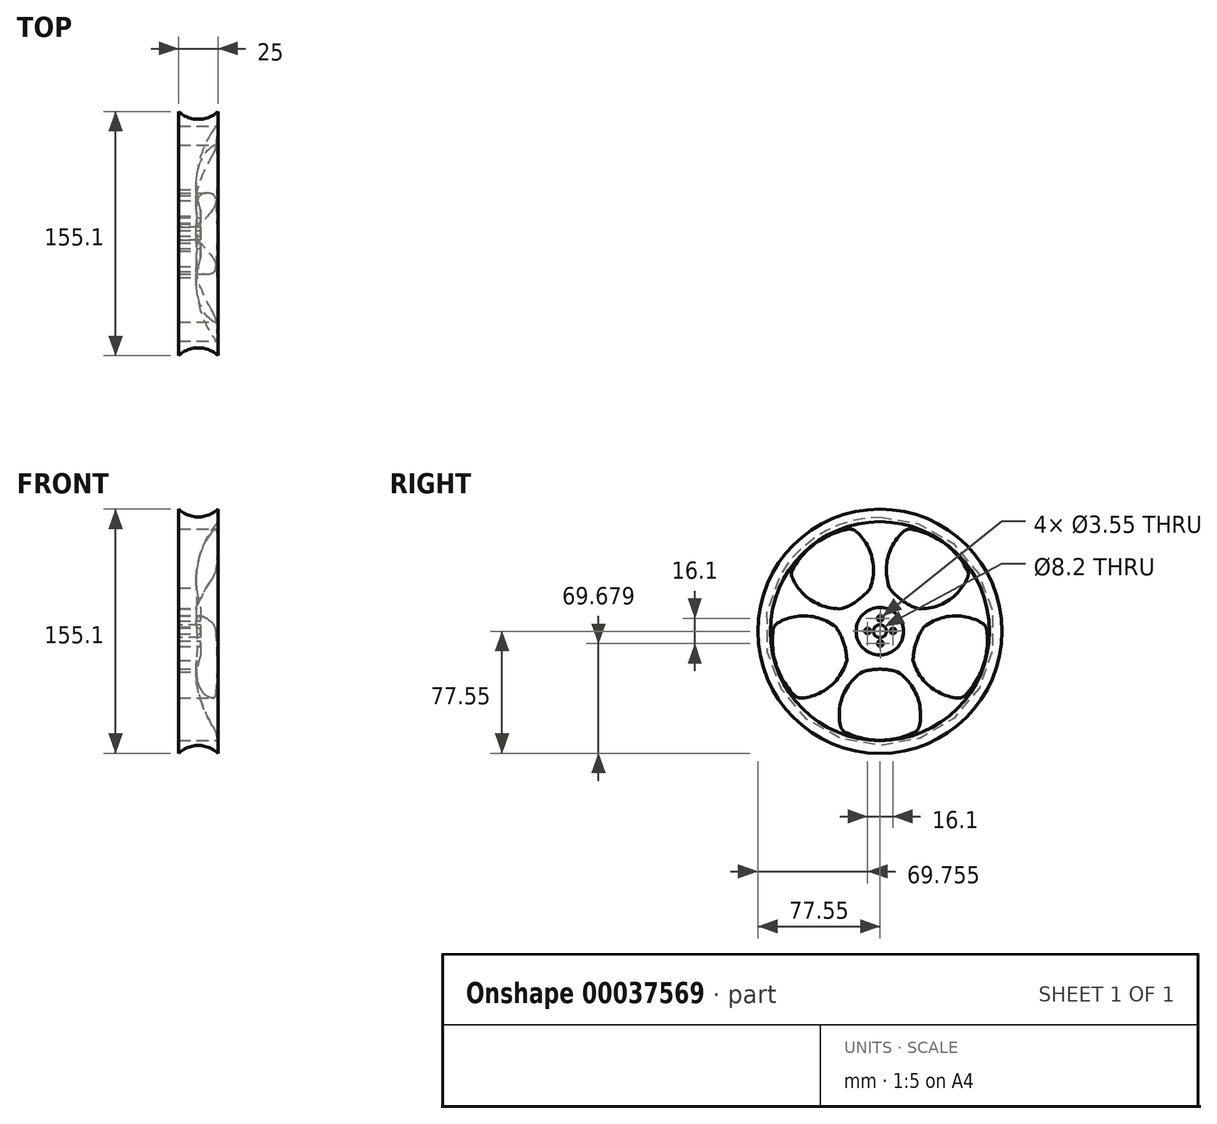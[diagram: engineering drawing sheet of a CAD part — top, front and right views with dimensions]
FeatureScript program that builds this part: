
annotation { "Feature Type Name" : "Feature", "Feature Type Description" : "" }
export const myFeature = defineFeature(function(context is Context, id is Id, definition is map)
    precondition{}
    {
        {
            var Q0;
            Q0=qCreatedBy(makeId("Top.planeOp"),FACE);
            var sketch = newSketch(context, id + "F0", { "sketchPlane" : qUnion([Q0])});
            skLineSegment(sketch, "E0", {"start": v(-41.62, 0) * mm, "end": v(49.27, 0) * mm, "construction": true});
            skLineSegment(sketch, "E1", {"start": v(0, 0) * mm, "end": v(0, 26.1) * mm, "construction": true});
            skLineSegment(sketch, "E2", {"start": v(-10.94, 77.55) * mm, "end": v(-10.94, 4.1) * mm});
            skArc(sketch, "E3", {"start": v(-10.94, 77.55) * mm, "mid": v(1.56, 72.59) * mm, "end": v(14.06, 77.55) * mm});
            skLineSegment(sketch, "E4", {"start": v(14.06, 77.55) * mm, "end": v(14.06, 69.55) * mm});
            skArc(sketch, "E5", {"start": v(14.06, 69.55) * mm, "mid": v(1.38, 43.78) * mm, "end": v(3.06, 15.1) * mm});
            skLineSegment(sketch, "E6", {"start": v(3.06, 15.1) * mm, "end": v(3.06, 4.1) * mm});
            skLineSegment(sketch, "E7", {"start": v(3.06, 4.1) * mm, "end": v(-10.94, 4.1) * mm});
            skSolve(sketch);
        }
        {
            var Q0;
            Q0=makeQuery(id+"F0.imprint","IMPRINT",FACE,{"disambiguationData":[TD([[makeQuery(id+"F0.imprint","IMPRINT",EDGE,{"derivedFrom":sQuery(id+"F0.wireOp",EDGE,"E2")}),1.0]])]});
            var Q1;
            Q1=sQuery(id+"F0.wireOp",EDGE,"E0");
            revolve(context, id + "F1", {"entities" : qUnion([Q0]), "axis" : qUnion([Q1]), "revolveType" : RevolveType.FULL});
        }
        {
            var Q0;
            Q0=qCreatedBy(makeId("Right.planeOp"),FACE);
            cPlane(context, id + "F2", {"entities" : qUnion([Q0]), "cplaneType" : CPlaneType.OFFSET, "offset" : 15 * mm, "width" : 150 * mm, "height" : 150 * mm});
        }
        {
            var Q0;
            Q0=qCreatedBy(id+"F2.planeOp",FACE);
            var sketch = newSketch(context, id + "F3", { "sketchPlane" : qUnion([Q0])});
            skArc(sketch, "E8", {"start": v(-11.09, -25.74) * mm, "mid": v(-23.44, -40.77) * mm, "end": v(-25.05, -60.15) * mm});
            skArc(sketch, "E9.MirrorCS", {"start": v(11.09, -25.74) * mm, "mid": v(23.44, -40.77) * mm, "end": v(25.05, -60.15) * mm});
            skArc(sketch, "E10", {"start": v(11.09, -25.74) * mm, "mid": v(0, -24.1) * mm, "end": v(-11.09, -25.74) * mm});
            skArc(sketch, "E11", {"start": v(-21.8, -64.25) * mm, "mid": v(0, -69.23) * mm, "end": v(21.8, -64.25) * mm});
            skPoint(sketch, "E12.visualSharp", {"position": v(-24.29, -62.96) * mm});
            skArc(sketch, "E12.filletArc", {"start": v(-25.05, -60.15) * mm, "mid": v(-23.9, -62.57) * mm, "end": v(-21.8, -64.25) * mm});
            skPoint(sketch, "E13.visualSharp", {"position": v(24.29, -62.96) * mm});
            skArc(sketch, "E13.filletArc", {"start": v(21.8, -64.25) * mm, "mid": v(23.9, -62.57) * mm, "end": v(25.05, -60.15) * mm});
            skArc(sketch, "E14.1.0", {"start": v(27.9, 2.6) * mm, "mid": v(22.92, -7.45) * mm, "end": v(21.05, -18.5) * mm});
            skArc(sketch, "E14.1.1", {"start": v(27.9, 2.6) * mm, "mid": v(46.01, 9.7) * mm, "end": v(64.95, 5.23) * mm});
            skArc(sketch, "E14.1.2", {"start": v(54.37, -40.59) * mm, "mid": v(65.84, -21.4) * mm, "end": v(67.84, 0.88) * mm});
            skArc(sketch, "E14.1.3", {"start": v(21.05, -18.5) * mm, "mid": v(31.53, -34.89) * mm, "end": v(49.47, -42.4) * mm});
            skArc(sketch, "E14.1.4", {"start": v(67.84, 0.88) * mm, "mid": v(66.9, 3.39) * mm, "end": v(64.95, 5.23) * mm});
            skArc(sketch, "E14.1.5", {"start": v(49.47, -42.4) * mm, "mid": v(52.13, -42.06) * mm, "end": v(54.37, -40.59) * mm});
            skArc(sketch, "E14.2.0", {"start": v(6.16, 27.34) * mm, "mid": v(14.16, 19.5) * mm, "end": v(24.1, 14.3) * mm});
            skArc(sketch, "E14.2.1", {"start": v(6.16, 27.34) * mm, "mid": v(5, 46.76) * mm, "end": v(15.1, 63.39) * mm});
            skArc(sketch, "E14.2.2", {"start": v(55.4, 39.17) * mm, "mid": v(40.7, 56) * mm, "end": v(20.13, 64.8) * mm});
            skArc(sketch, "E14.2.3", {"start": v(24.1, 14.3) * mm, "mid": v(42.92, 19.2) * mm, "end": v(55.62, 33.94) * mm});
            skArc(sketch, "E14.2.4", {"start": v(20.13, 64.8) * mm, "mid": v(17.45, 64.67) * mm, "end": v(15.1, 63.39) * mm});
            skArc(sketch, "E14.2.5", {"start": v(55.62, 33.94) * mm, "mid": v(56.1, 36.58) * mm, "end": v(55.4, 39.17) * mm});
            skArc(sketch, "E14.3.0", {"start": v(-24.1, 14.3) * mm, "mid": v(-14.16, 19.5) * mm, "end": v(-6.16, 27.34) * mm});
            skArc(sketch, "E14.3.1", {"start": v(-24.1, 14.3) * mm, "mid": v(-42.92, 19.2) * mm, "end": v(-55.62, 33.94) * mm});
            skArc(sketch, "E14.3.2", {"start": v(-20.13, 64.8) * mm, "mid": v(-40.7, 56) * mm, "end": v(-55.4, 39.17) * mm});
            skArc(sketch, "E14.3.3", {"start": v(-6.16, 27.34) * mm, "mid": v(-5, 46.76) * mm, "end": v(-15.1, 63.39) * mm});
            skArc(sketch, "E14.3.4", {"start": v(-55.4, 39.17) * mm, "mid": v(-56.1, 36.58) * mm, "end": v(-55.62, 33.94) * mm});
            skArc(sketch, "E14.3.5", {"start": v(-15.1, 63.39) * mm, "mid": v(-17.45, 64.67) * mm, "end": v(-20.13, 64.8) * mm});
            skArc(sketch, "E14.4.0", {"start": v(-21.05, -18.5) * mm, "mid": v(-22.92, -7.45) * mm, "end": v(-27.9, 2.6) * mm});
            skArc(sketch, "E14.4.1", {"start": v(-21.05, -18.5) * mm, "mid": v(-31.53, -34.89) * mm, "end": v(-49.47, -42.4) * mm});
            skArc(sketch, "E14.4.2", {"start": v(-67.84, 0.88) * mm, "mid": v(-65.84, -21.4) * mm, "end": v(-54.37, -40.59) * mm});
            skArc(sketch, "E14.4.3", {"start": v(-27.9, 2.6) * mm, "mid": v(-46.01, 9.7) * mm, "end": v(-64.95, 5.23) * mm});
            skArc(sketch, "E14.4.4", {"start": v(-54.37, -40.59) * mm, "mid": v(-52.13, -42.06) * mm, "end": v(-49.47, -42.4) * mm});
            skArc(sketch, "E14.4.5", {"start": v(-64.95, 5.23) * mm, "mid": v(-66.9, 3.39) * mm, "end": v(-67.84, 0.88) * mm});
            skPoint(sketch, "E14.center", {"position": v(0, 0) * mm});
            skCircle(sketch, "E15.1.0", {"center": v(-7.8, 0.18) * mm, "radius": 1.77 * mm});
            skCircle(sketch, "E16", {"center": v(0.25, 8.23) * mm, "radius": 1.77 * mm});
            skCircle(sketch, "E15.3.0", {"center": v(8.3, 0.18) * mm, "radius": 1.77 * mm});
            skCircle(sketch, "E15.2.0", {"center": v(0.25, -7.87) * mm, "radius": 1.77 * mm});
            skSolve(sketch);
        }
        {
            var Q0;
            Q0=makeQuery(id+"F3.imprint","IMPRINT",FACE,{"disambiguationData":[TD([[makeQuery(id+"F3.imprint","IMPRINT",EDGE,{"derivedFrom":sQuery(id+"F3.wireOp",EDGE,"E14.4.0")}),1.0]])]});
            var Q1;
            Q1=makeQuery(id+"F3.imprint","IMPRINT",FACE,{"disambiguationData":[TD([[makeQuery(id+"F3.imprint","IMPRINT",EDGE,{"derivedFrom":sQuery(id+"F3.wireOp",EDGE,"E14.3.0")}),1.0]])]});
            var Q2;
            Q2=makeQuery(id+"F3.imprint","IMPRINT",FACE,{"disambiguationData":[TD([[makeQuery(id+"F3.imprint","IMPRINT",EDGE,{"derivedFrom":sQuery(id+"F3.wireOp",EDGE,"E14.2.0")}),1.0]])]});
            var Q3;
            Q3=makeQuery(id+"F3.imprint","IMPRINT",FACE,{"disambiguationData":[TD([[makeQuery(id+"F3.imprint","IMPRINT",EDGE,{"derivedFrom":sQuery(id+"F3.wireOp",EDGE,"E14.1.0")}),1.0]])]});
            var Q4;
            Q4=makeQuery(id+"F3.imprint","IMPRINT",FACE,{"disambiguationData":[TD([[makeQuery(id+"F3.imprint","IMPRINT",EDGE,{"derivedFrom":sQuery(id+"F3.wireOp",EDGE,"E8")}),1.0]])]});
            var Q5;
            Q5=makeQuery(id+"F3.imprint","IMPRINT",FACE,{"disambiguationData":[TD([[makeQuery(id+"F3.imprint","IMPRINT",EDGE,{"derivedFrom":sQuery(id+"F3.wireOp",EDGE,"E16")}),1.0]])]});
            var Q6;
            Q6=makeQuery(id+"F3.imprint","IMPRINT",FACE,{"disambiguationData":[TD([[makeQuery(id+"F3.imprint","IMPRINT",EDGE,{"derivedFrom":sQuery(id+"F3.wireOp",EDGE,"E15.3.0")}),1.0]])]});
            var Q7;
            Q7=makeQuery(id+"F3.imprint","IMPRINT",FACE,{"disambiguationData":[TD([[makeQuery(id+"F3.imprint","IMPRINT",EDGE,{"derivedFrom":sQuery(id+"F3.wireOp",EDGE,"E15.2.0")}),1.0]])]});
            var Q8;
            Q8=makeQuery(id+"F3.imprint","IMPRINT",FACE,{"disambiguationData":[TD([[makeQuery(id+"F3.imprint","IMPRINT",EDGE,{"derivedFrom":sQuery(id+"F3.wireOp",EDGE,"E15.1.0")}),1.0]])]});
            extrude(context, id + "F4", {"entities" : qUnion([Q0, Q1, Q2, Q3, Q4, Q5, Q6, Q7, Q8]), "operationType" : NewBodyOperationType.REMOVE, "oppositeDirection" : true, "depth" : 50 * mm});
        }
    });
